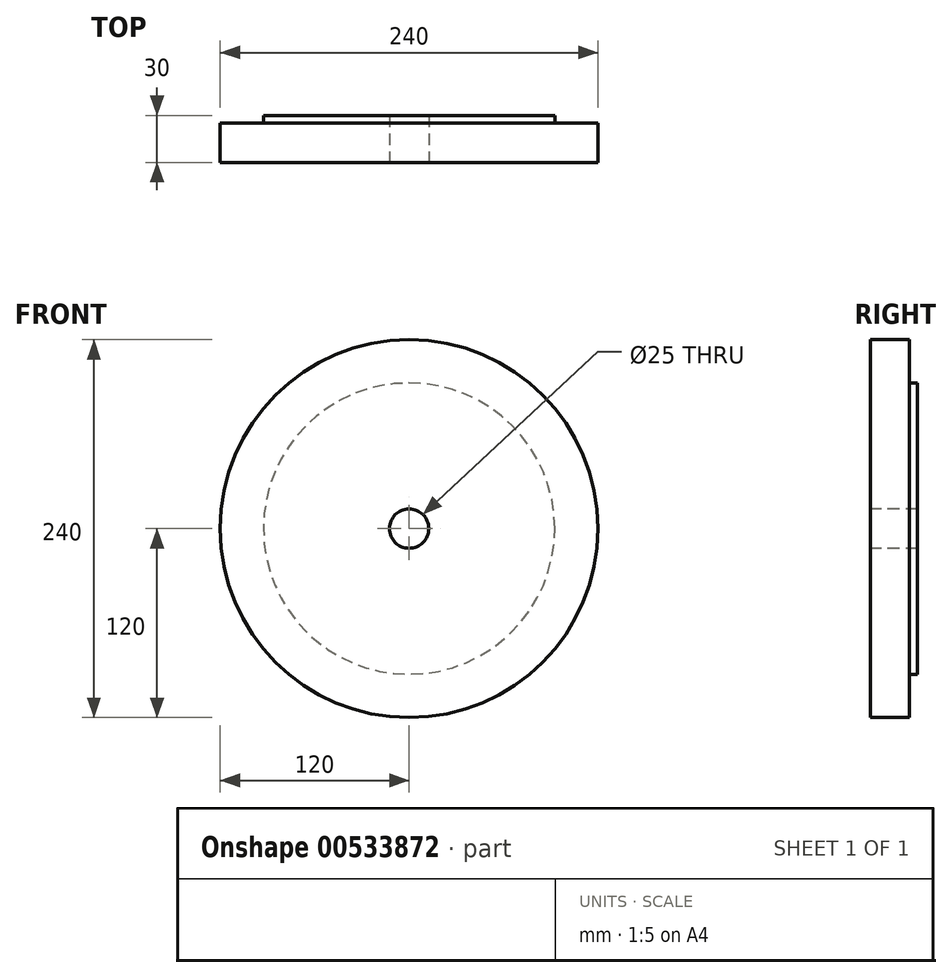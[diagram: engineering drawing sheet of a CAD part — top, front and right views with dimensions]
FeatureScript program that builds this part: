
annotation { "Feature Type Name" : "Feature", "Feature Type Description" : "" }
export const myFeature = defineFeature(function(context is Context, id is Id, definition is map)
    precondition{}
    {
        {
            var Q0;
            Q0=qCreatedBy(makeId("Front.planeOp"),FACE);
            var sketch = newSketch(context, id + "F0", { "sketchPlane" : qUnion([Q0])});
            skCircle(sketch, "E0", {"center": v(0, 0) * mm, "radius": 92.5 * mm});
            skSolve(sketch);
        }
        {
            var Q0;
            Q0=makeQuery(id+"F0.imprint","IMPRINT",FACE,{"disambiguationData":[TD([[makeQuery(id+"F0.imprint","IMPRINT",EDGE,{"derivedFrom":sQuery(id+"F0.wireOp",EDGE,"E0")}),1.0]])]});
            extrude(context, id + "F1", {"entities" : qUnion([Q0]), "depth" : 5 * mm, "offsetDistance" : 25 * mm});
        }
        {
            var Q0;
            Q0=makeQuery(id+"F1.opExtrude","CAP_FACE",FACE,{"disambiguationData":[OSD([sQuery(id+"F0.wireOp",EDGE,"E0")])],"isStart":false});
            var sketch = newSketch(context, id + "F2", { "sketchPlane" : qUnion([Q0])});
            skCircle(sketch, "E1", {"center": v(0, 0) * mm, "radius": 120 * mm});
            skSolve(sketch);
        }
        {
            var Q0;
            Q0 = qSketchRegion(id + "F2", true);
            extrude(context, id + "F3", {"entities" : qUnion([Q0]), "operationType" : NewBodyOperationType.ADD, "depth" : 25 * mm, "offsetDistance" : 25 * mm});
        }
        {
            var Q0;
            Q0=makeQuery(id+"F3.opExtrude","CAP_FACE",FACE,{"disambiguationData":[OSD([sQuery(id+"F2.wireOp",EDGE,"E1")])],"isStart":false});
            var sketch = newSketch(context, id + "F4", { "sketchPlane" : qUnion([Q0])});
            skCircle(sketch, "E2", {"center": v(0, 0) * mm, "radius": 12.5 * mm});
            skSolve(sketch);
        }
        {
            var Q0;
            Q0=makeQuery(id+"F4.imprint","IMPRINT",FACE,{"disambiguationData":[TD([[makeQuery(id+"F4.imprint","IMPRINT",EDGE,{"derivedFrom":sQuery(id+"F4.wireOp",EDGE,"E2")}),1.0]])]});
            extrude(context, id + "F5", {"entities" : qUnion([Q0]), "operationType" : NewBodyOperationType.REMOVE, "oppositeDirection" : true, "depth" : 76 * mm, "offsetDistance" : 25 * mm});
        }
    });
